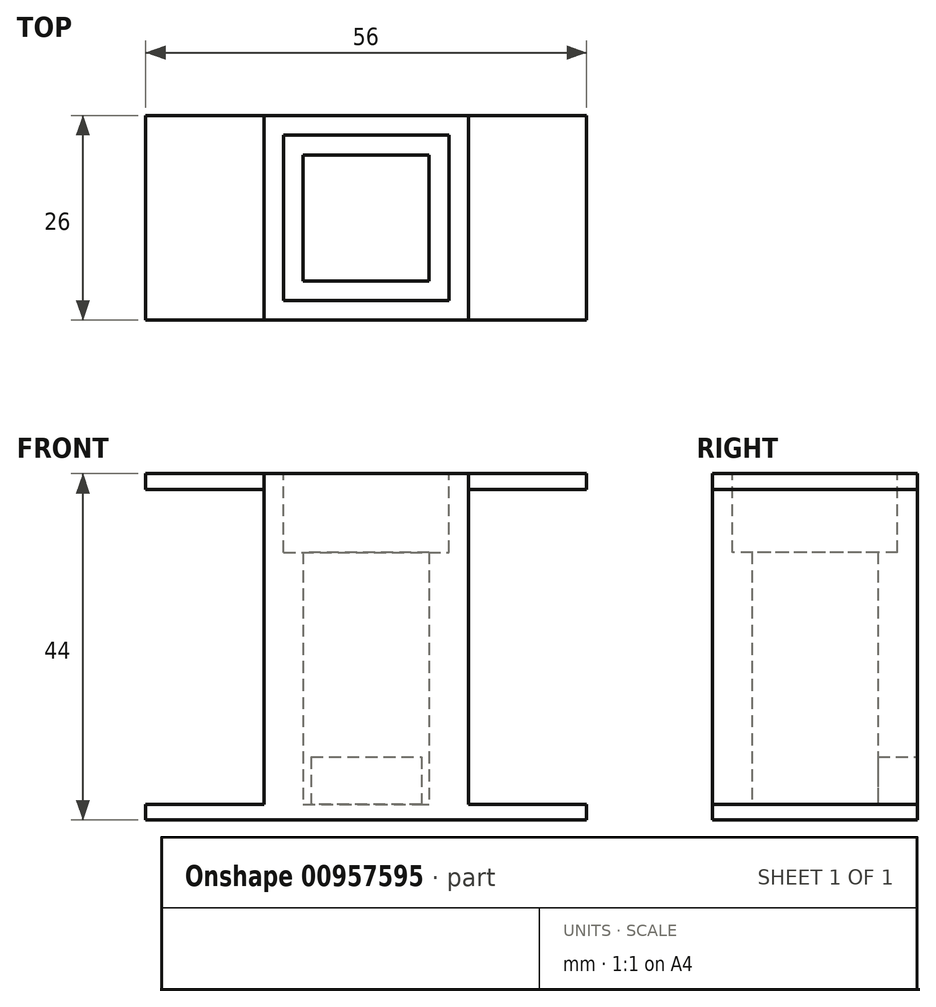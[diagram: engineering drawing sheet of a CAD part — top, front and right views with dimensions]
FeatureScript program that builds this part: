
annotation { "Feature Type Name" : "Feature", "Feature Type Description" : "" }
export const myFeature = defineFeature(function(context is Context, id is Id, definition is map)
    precondition{}
    {
        {
            var Q0;
            Q0=qCreatedBy(makeId("Top.planeOp"),FACE);
            var sketch = newSketch(context, id + "F0", { "sketchPlane" : qUnion([Q0])});
            skLineSegment(sketch, "E0.bottom", {"start": v(13, 13) * mm, "end": v(-13, 13) * mm});
            skLineSegment(sketch, "E0.top", {"start": v(13, -13) * mm, "end": v(-13, -13) * mm});
            skLineSegment(sketch, "E0.left", {"start": v(13, 13) * mm, "end": v(13, -13) * mm});
            skLineSegment(sketch, "E0.right", {"start": v(-13, 13) * mm, "end": v(-13, -13) * mm});
            skPoint(sketch, "E0.middle", {"position": v(0, 0) * mm});
            skLineSegment(sketch, "E1.bottom", {"start": v(8, 8) * mm, "end": v(-8, 8) * mm});
            skLineSegment(sketch, "E1.top", {"start": v(8, -8) * mm, "end": v(-8, -8) * mm});
            skLineSegment(sketch, "E1.left", {"start": v(8, 8) * mm, "end": v(8, -8) * mm});
            skLineSegment(sketch, "E1.right", {"start": v(-8, 8) * mm, "end": v(-8, -8) * mm});
            skSolve(sketch);
        }
        {
            var Q0;
            Q0=makeQuery(id+"F0.imprint","IMPRINT",FACE,{"disambiguationData":[TD([[makeQuery(id+"F0.imprint","IMPRINT",EDGE,{"derivedFrom":sQuery(id+"F0.wireOp",EDGE,"E0.bottom")}),1.0]])]});
            var Q1;
            Q1=makeQuery(id+"F0.imprint","IMPRINT",FACE,{"disambiguationData":[TD([[makeQuery(id+"F0.imprint","IMPRINT",EDGE,{"derivedFrom":sQuery(id+"F0.wireOp",EDGE,"E1.bottom")}),-1.0]])]});
            var Q2;
            Q2=makeQuery(id+"F0.imprint","IMPRINT",FACE,{"disambiguationData":[TD([[makeQuery(id+"F0.imprint","IMPRINT",EDGE,{"derivedFrom":sQuery(id+"F0.wireOp",EDGE,"E1.bottom")}),1.0]])]});
            extrude(context, id + "F1", {"entities" : qUnion([Q0, Q1, Q2]), "depth" : 2 * mm, "offsetDistance" : 25 * mm});
        }
        {
            var Q0;
            Q0=qSketchRegion(id+"F0",true);
            var Q1;
            Q1=makeQuery(id+"F0.imprint","IMPRINT",FACE,{"disambiguationData":[TD([[makeQuery(id+"F0.imprint","IMPRINT",EDGE,{"derivedFrom":sQuery(id+"F0.wireOp",EDGE,"E1.bottom")}),-1.0]])]});
            extrude(context, id + "F2", {"entities" : qUnion([Q0, Q1]), "operationType" : NewBodyOperationType.ADD, "depth" : 40 * mm, "offsetDistance" : 25 * mm});
        }
        {
            var Q0;
            Q0=makeQuery(id+"F2.opExtrude","CAP_FACE",FACE,{"disambiguationData":[OSD([sQuery(id+"F0.wireOp",EDGE,"E0.bottom"),sQuery(id+"F0.wireOp",EDGE,"E0.top"),sQuery(id+"F0.wireOp",EDGE,"E0.left"),sQuery(id+"F0.wireOp",EDGE,"E0.right"),sQuery(id+"F0.wireOp",EDGE,"E1.bottom"),sQuery(id+"F0.wireOp",EDGE,"E1.top"),sQuery(id+"F0.wireOp",EDGE,"E1.left"),sQuery(id+"F0.wireOp",EDGE,"E1.right")])],"isStart":false});
            var sketch = newSketch(context, id + "F3", { "sketchPlane" : qUnion([Q0])});
            skLineSegment(sketch, "E2.bottom", {"start": v(-9, 9) * mm, "end": v(9, 9) * mm});
            skLineSegment(sketch, "E2.top", {"start": v(-9, -9) * mm, "end": v(9, -9) * mm});
            skLineSegment(sketch, "E2.left", {"start": v(-9, 9) * mm, "end": v(-9, -9) * mm});
            skLineSegment(sketch, "E2.right", {"start": v(9, 9) * mm, "end": v(9, -9) * mm});
            skPoint(sketch, "E2.middle", {"position": v(0, 0) * mm});
            skSolve(sketch);
        }
        {
            var Q0;
            Q0=makeQuery(id+"F3.imprint","IMPRINT",FACE,{"disambiguationData":[TD([[makeQuery(id+"F3.imprint","IMPRINT",EDGE,{"derivedFrom":sQuery(id+"F3.wireOp",EDGE,"E2.bottom")}),1.0]])]});
            extrude(context, id + "F4", {"entities" : qUnion([Q0]), "operationType" : NewBodyOperationType.ADD, "depth" : 4 * mm, "offsetDistance" : 25 * mm});
        }
        {
            var Q0;
            Q0=makeQuery(id+"F4.opExtrude","CAP_FACE",FACE,{"disambiguationData":[OSD([sQuery(id+"F0.wireOp",EDGE,"E0.bottom"),sQuery(id+"F0.wireOp",EDGE,"E0.top"),sQuery(id+"F0.wireOp",EDGE,"E0.left"),sQuery(id+"F0.wireOp",EDGE,"E0.right"),sQuery(id+"F3.wireOp",EDGE,"E2.bottom"),sQuery(id+"F3.wireOp",EDGE,"E2.top"),sQuery(id+"F3.wireOp",EDGE,"E2.left"),sQuery(id+"F3.wireOp",EDGE,"E2.right")])],"isStart":false});
            var sketch = newSketch(context, id + "F5", { "sketchPlane" : qUnion([Q0])});
            skLineSegment(sketch, "E3", {"start": v(-2.5, 13) * mm, "end": v(-2.5, 9) * mm});
            skLineSegment(sketch, "E4.MirrorCS", {"start": v(2.5, 13) * mm, "end": v(2.5, 9) * mm});
            skLineSegment(sketch, "E5.MirrorCS", {"start": v(2.5, -13) * mm, "end": v(2.5, -9) * mm});
            skLineSegment(sketch, "E6.MirrorCS", {"start": v(-2.5, -13) * mm, "end": v(-2.5, -9) * mm});
            skLineSegment(sketch, "E7", {"start": v(-13, 13) * mm, "end": v(-9, 9) * mm, "construction": true});
            skPoint(sketch, "E8", {"position": v(-10.5, 10.5) * mm});
            skPoint(sketch, "E9.MirrorP", {"position": v(10.5, 10.5) * mm});
            skLineSegment(sketch, "E10.MirrorCS", {"start": v(13, 13) * mm, "end": v(9, 9) * mm, "construction": true});
            skLineSegment(sketch, "E11.MirrorCS", {"start": v(-13, -13) * mm, "end": v(-9, -9) * mm, "construction": true});
            skPoint(sketch, "E12.MirrorP", {"position": v(-10.5, -10.5) * mm});
            skLineSegment(sketch, "E13.MirrorCS", {"start": v(13, -13) * mm, "end": v(9, -9) * mm, "construction": true});
            skPoint(sketch, "E14.MirrorP", {"position": v(10.5, -10.5) * mm});
            skSolve(sketch);
        }
        {
            var Q0;
            {var subQ0=sQuery(id+"F0.wireOp",EDGE,"E0.left");Q0=makeQuery(id+"F4.boolean.opBoolean","MERGE",FACE,{"derivedFrom":[makeQuery(id+"F2.boolean.opBoolean","MERGE",FACE,{"derivedFrom":[makeQuery(id+"F1.opExtrude","SWEPT_FACE",FACE,{"disambiguationData":[OSD([subQ0])]}),makeQuery(id+"F2.opExtrude","SWEPT_FACE",FACE,{"disambiguationData":[OSD([subQ0])]})]}),makeQuery(id+"F4.opExtrude","SWEPT_FACE",FACE,{"disambiguationData":[OSD([subQ0])]})]});}
            var sketch = newSketch(context, id + "F6", { "sketchPlane" : qUnion([Q0])});
            skLineSegment(sketch, "E15.bottom", {"start": v(-7.98, 38) * mm, "end": v(8.02, 38) * mm});
            skLineSegment(sketch, "E15.top", {"start": v(-7.98, 2) * mm, "end": v(8.02, 2) * mm});
            skLineSegment(sketch, "E15.left", {"start": v(-7.98, 38) * mm, "end": v(-7.98, 2) * mm});
            skLineSegment(sketch, "E15.right", {"start": v(8.02, 38) * mm, "end": v(8.02, 2) * mm});
            skLineSegment(sketch, "E16", {"start": v(-7.98, 0) * mm, "end": v(-7.98, 40) * mm, "construction": true});
            skLineSegment(sketch, "E17", {"start": v(8.02, 0) * mm, "end": v(8.02, 40) * mm, "construction": true});
            skSolve(sketch);
        }
        {
            var Q0;
            {var subQ0=sQuery(id+"F0.wireOp",EDGE,"E0.bottom");Q0=makeQuery(id+"F4.boolean.opBoolean","MERGE",FACE,{"derivedFrom":[makeQuery(id+"F2.boolean.opBoolean","MERGE",FACE,{"derivedFrom":[makeQuery(id+"F1.opExtrude","SWEPT_FACE",FACE,{"disambiguationData":[OSD([subQ0])]}),makeQuery(id+"F2.opExtrude","SWEPT_FACE",FACE,{"disambiguationData":[OSD([subQ0])]})]}),makeQuery(id+"F4.opExtrude","SWEPT_FACE",FACE,{"disambiguationData":[OSD([subQ0])]})]});}
            var sketch = newSketch(context, id + "F7", { "sketchPlane" : qUnion([Q0])});
            skLineSegment(sketch, "E18.bottom", {"start": v(-7, 2) * mm, "end": v(7, 2) * mm});
            skLineSegment(sketch, "E18.top", {"start": v(-7, 8) * mm, "end": v(7, 8) * mm});
            skLineSegment(sketch, "E18.left", {"start": v(-7, 2) * mm, "end": v(-7, 8) * mm});
            skLineSegment(sketch, "E18.right", {"start": v(7, 2) * mm, "end": v(7, 8) * mm});
            skSolve(sketch);
        }
        {
            var Q0;
            Q0=makeQuery(id+"F7.imprint","IMPRINT",FACE,{"disambiguationData":[TD([[makeQuery(id+"F7.imprint","IMPRINT",EDGE,{"derivedFrom":sQuery(id+"F7.wireOp",EDGE,"E18.bottom")}),1.0]])]});
            extrude(context, id + "F8", {"entities" : qUnion([Q0]), "operationType" : NewBodyOperationType.REMOVE, "oppositeDirection" : true, "depth" : 15.3 * mm, "offsetDistance" : 25 * mm});
        }
        {
            var Q0;
            {var subQ5=sQuery(id+"F5.wireOp",EDGE,"E3");Q0=makeQuery(id+"F5.imprint","IMPRINT",FACE,{"disambiguationData":[TD([[makeQuery(id+"F5.imprint","IMPRINT",EDGE,{"derivedFrom":subQ5}),-1.0]])]});}
            var sketch = newSketch(context, id + "F9", { "sketchPlane" : qUnion([Q0])});
            skLineSegment(sketch, "E19.bottom", {"start": v(-13, 13) * mm, "end": v(-28, 13) * mm});
            skLineSegment(sketch, "E19.top", {"start": v(-13, -13) * mm, "end": v(-28, -13) * mm});
            skLineSegment(sketch, "E19.left", {"start": v(-13, 13) * mm, "end": v(-13, -13) * mm});
            skLineSegment(sketch, "E19.right", {"start": v(-28, 13) * mm, "end": v(-28, -13) * mm});
            skLineSegment(sketch, "E20.bottom", {"start": v(13, 13) * mm, "end": v(28, 13) * mm});
            skLineSegment(sketch, "E20.top", {"start": v(13, -13) * mm, "end": v(28, -13) * mm});
            skLineSegment(sketch, "E20.left", {"start": v(13, 13) * mm, "end": v(13, -13) * mm});
            skLineSegment(sketch, "E20.right", {"start": v(28, 13) * mm, "end": v(28, -13) * mm});
            skSolve(sketch);
        }
        {
            var Q0;
            Q0=makeQuery(id+"F9.imprint","IMPRINT",FACE,{"disambiguationData":[TD([[makeQuery(id+"F9.imprint","IMPRINT",EDGE,{"derivedFrom":sQuery(id+"F9.wireOp",EDGE,"E19.bottom")}),1.0]])]});
            var Q1;
            Q1=makeQuery(id+"F9.imprint","IMPRINT",FACE,{"disambiguationData":[TD([[makeQuery(id+"F9.imprint","IMPRINT",EDGE,{"derivedFrom":sQuery(id+"F9.wireOp",EDGE,"E20.bottom")}),-1.0]])]});
            extrude(context, id + "F10", {"entities" : qUnion([Q0, Q1]), "oppositeDirection" : true, "depth" : 2 * mm, "offsetDistance" : 25 * mm});
        }
        {
            var Q0;
            Q0=makeQuery(id+"F0.imprint","IMPRINT",FACE,{"disambiguationData":[TD([[makeQuery(id+"F0.imprint","IMPRINT",EDGE,{"derivedFrom":sQuery(id+"F0.wireOp",EDGE,"E0.bottom")}),1.0]])]});
            var sketch = newSketch(context, id + "F11", { "sketchPlane" : qUnion([Q0])});
            skLineSegment(sketch, "E21.bottom", {"start": v(-13, -13) * mm, "end": v(-28, -13) * mm});
            skLineSegment(sketch, "E21.top", {"start": v(-13, 13) * mm, "end": v(-28, 13) * mm});
            skLineSegment(sketch, "E21.left", {"start": v(-13, -13) * mm, "end": v(-13, 13) * mm});
            skLineSegment(sketch, "E21.right", {"start": v(-28, -13) * mm, "end": v(-28, 13) * mm});
            skLineSegment(sketch, "E22.bottom", {"start": v(13, -13) * mm, "end": v(28, -13) * mm});
            skLineSegment(sketch, "E22.top", {"start": v(13, 13) * mm, "end": v(28, 13) * mm});
            skLineSegment(sketch, "E22.left", {"start": v(13, -13) * mm, "end": v(13, 13) * mm});
            skLineSegment(sketch, "E22.right", {"start": v(28, -13) * mm, "end": v(28, 13) * mm});
            skSolve(sketch);
        }
        {
            var Q0;
            Q0 = qSketchRegion(id + "F11", true);
            extrude(context, id + "F12", {"entities" : qUnion([Q0]), "operationType" : NewBodyOperationType.ADD, "depth" : 2 * mm, "offsetDistance" : 25 * mm});
        }
        {
            var Q0;
            {var subQ5=sQuery(id+"F5.wireOp",EDGE,"E3");Q0=makeQuery(id+"F5.imprint","IMPRINT",FACE,{"disambiguationData":[TD([[makeQuery(id+"F5.imprint","IMPRINT",EDGE,{"derivedFrom":subQ5}),-1.0]])]});}
            var sketch = newSketch(context, id + "F13", { "sketchPlane" : qUnion([Q0])});
            skLineSegment(sketch, "E23.bottom", {"start": v(-10.5, 10.5) * mm, "end": v(10.5, 10.5) * mm});
            skLineSegment(sketch, "E23.top", {"start": v(-10.5, -10.5) * mm, "end": v(10.5, -10.5) * mm});
            skLineSegment(sketch, "E23.left", {"start": v(-10.5, 10.5) * mm, "end": v(-10.5, -10.5) * mm});
            skLineSegment(sketch, "E23.right", {"start": v(10.5, 10.5) * mm, "end": v(10.5, -10.5) * mm});
            skSolve(sketch);
        }
        {
            var Q0;
            Q0 = qSketchRegion(id + "F13", true);
            extrude(context, id + "F14", {"entities" : qUnion([Q0]), "operationType" : NewBodyOperationType.REMOVE, "oppositeDirection" : true, "depth" : 10 * mm, "offsetDistance" : 25 * mm});
        }
    });
